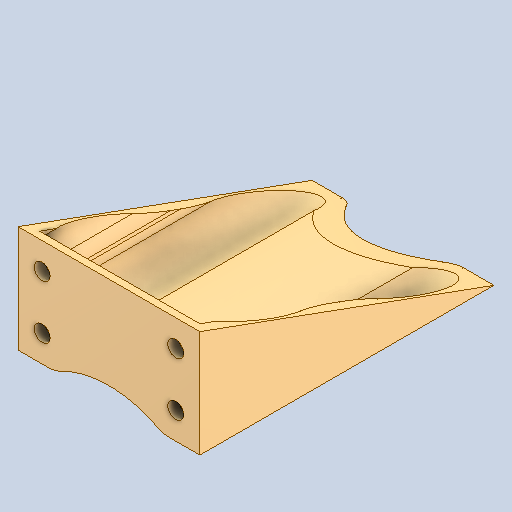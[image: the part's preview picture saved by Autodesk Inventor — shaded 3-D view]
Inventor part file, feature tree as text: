
AUTODESK INVENTOR PART (.ipt)
format: ipt  version: 2024.2 (Build 282272000, 272)  size: 140,800 bytes
history: native  units: in
note: dims shown in document units (in); Inventor stores cm internally (conversion verified against a paired STEP export)
features: other x1, fillet x1
ambient origin geometry x8: Origin, YZ Plane, XZ Plane, XY Plane, X Axis, Y Axis, Z Axis, Center Point
bodies: Solid1 (feature_tree)
feature tree (2):
  other  "Plano1"
  fillet  "Redondeo4"  [1 undecoded]
note: 1 required parameter value undecoded (feature->parameter linkage not recoverable at this tier; creation-order binding heuristic only, values carry confidence <= 0.55)
